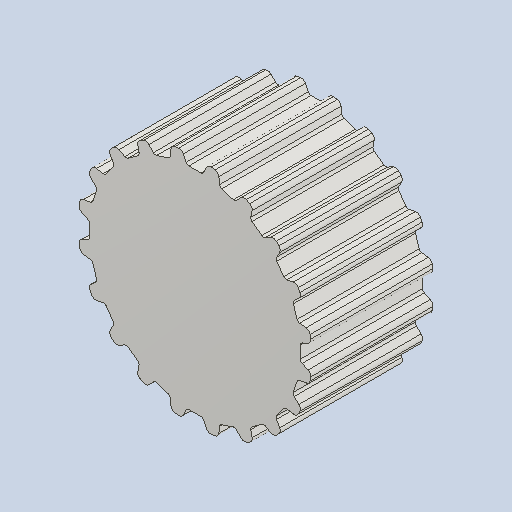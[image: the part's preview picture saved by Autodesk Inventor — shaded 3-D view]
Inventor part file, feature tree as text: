
AUTODESK INVENTOR PART (.ipt)
format: ipt  version: 2025.2 (Build 292293000, 293)  size: 252,928 bytes
history: native  units: mm (DEFAULTED — no unit token found)
features: other x3, extrude x2, fillet x1, pattern_circular x1
ambient origin geometry x8: Origin, YZ Plane, XZ Plane, XY Plane, X Axis, Y Axis, Z Axis, Center Point
bodies: Solid1 (feature_tree)
feature tree (7):
  other  "Pulley Sketch"
  extrude  "Base Body"  Depth=15.915494mm
  extrude  "Tooth"  Depth=0.3mm
  fillet  "Tooth Fillet"  Radius=0.75mm
  pattern_circular  "Teeth"  [2 undecoded]
  other  "Left flange"
  other  "Right flange"
note: 2 required parameter values undecoded (feature->parameter linkage not recoverable at this tier; creation-order binding heuristic only, values carry confidence <= 0.55)
